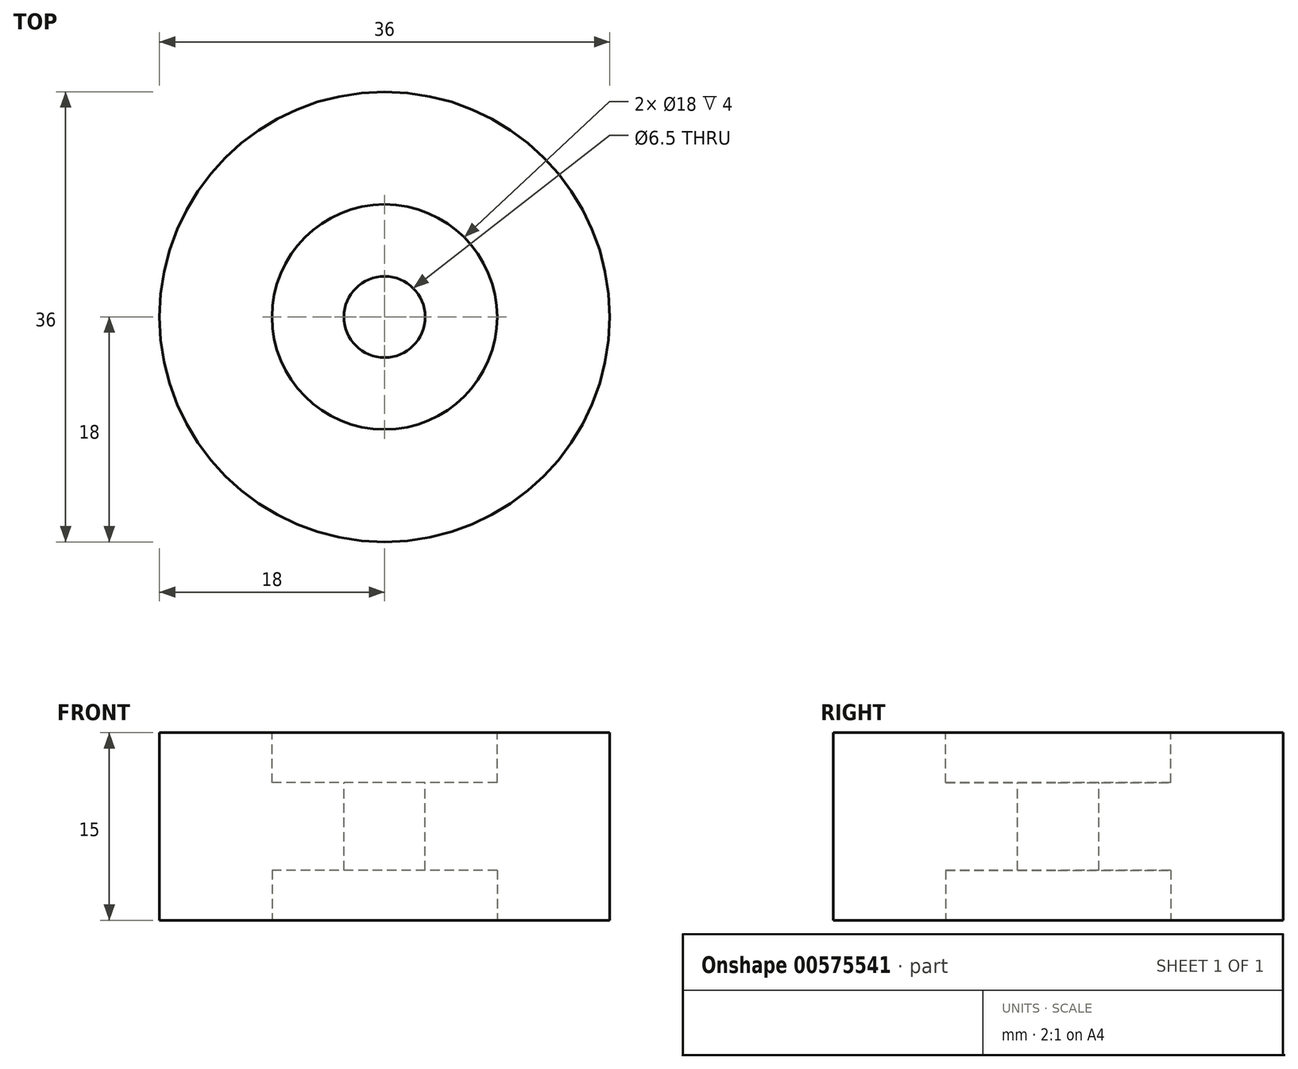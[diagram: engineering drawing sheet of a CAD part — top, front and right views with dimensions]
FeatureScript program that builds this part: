
annotation { "Feature Type Name" : "Feature", "Feature Type Description" : "" }
export const myFeature = defineFeature(function(context is Context, id is Id, definition is map)
    precondition{}
    {
        {
            var Q0;
            Q0=qCreatedBy(makeId("Top.planeOp"),FACE);
            var sketch = newSketch(context, id + "F0", { "sketchPlane" : qUnion([Q0])});
            skCircle(sketch, "E0", {"center": v(0, 0) * mm, "radius": 18 * mm});
            skSolve(sketch);
        }
        {
            var Q0;
            Q0=makeQuery(id+"F0.imprint","IMPRINT",FACE,{"disambiguationData":[TD([[makeQuery(id+"F0.imprint","IMPRINT",EDGE,{"derivedFrom":sQuery(id+"F0.wireOp",EDGE,"E0")}),1.0]])]});
            extrude(context, id + "F1", {"entities" : qUnion([Q0]), "depth" : 15 * mm, "offsetDistance" : 25 * mm});
        }
        {
            var Q0;
            Q0=makeQuery(id+"F1.opExtrude","CAP_FACE",FACE,{"disambiguationData":[OSD([sQuery(id+"F0.wireOp",EDGE,"E0")])],"isStart":false});
            var sketch = newSketch(context, id + "F2", { "sketchPlane" : qUnion([Q0])});
            skCircle(sketch, "E1", {"center": v(0, 0) * mm, "radius": 9 * mm});
            skCircle(sketch, "E2", {"center": v(0, 0) * mm, "radius": 3.25 * mm});
            skSolve(sketch);
        }
        {
            var Q0;
            Q0=makeQuery(id+"F2.imprint","IMPRINT",FACE,{"disambiguationData":[TD([[makeQuery(id+"F2.imprint","IMPRINT",EDGE,{"derivedFrom":sQuery(id+"F2.wireOp",EDGE,"E1")}),1.0]])]});
            var Q1;
            Q1=sQuery(id+"F2.wireOp",EDGE,"E1");
            extrude(context, id + "F3", {"entities" : qUnion([Q0]), "operationType" : NewBodyOperationType.REMOVE, "surfaceEntities" : qUnion([Q1]), "oppositeDirection" : true, "depth" : 4 * mm, "offsetDistance" : 25 * mm});
        }
        {
            var Q0;
            Q0=makeQuery(id+"F2.imprint","IMPRINT",FACE,{"disambiguationData":[TD([[makeQuery(id+"F2.imprint","IMPRINT",EDGE,{"derivedFrom":sQuery(id+"F2.wireOp",EDGE,"E2")}),1.0]])]});
            extrude(context, id + "F4", {"entities" : qUnion([Q0]), "operationType" : NewBodyOperationType.REMOVE, "oppositeDirection" : true, "depth" : 25 * mm, "offsetDistance" : 25 * mm});
        }
        {
            var Q0;
            Q0=makeQuery(id+"F0.imprint","IMPRINT",FACE,{"disambiguationData":[TD([[makeQuery(id+"F0.imprint","IMPRINT",EDGE,{"derivedFrom":sQuery(id+"F0.wireOp",EDGE,"E0")}),1.0]])]});
            var sketch = newSketch(context, id + "F5", { "sketchPlane" : qUnion([Q0])});
            skCircle(sketch, "E3", {"center": v(0, 0) * mm, "radius": 9 * mm});
            skSolve(sketch);
        }
        {
            var Q0;
            Q0=makeQuery(id+"F5.imprint","IMPRINT",FACE,{"disambiguationData":[TD([[makeQuery(id+"F5.imprint","IMPRINT",EDGE,{"derivedFrom":sQuery(id+"F5.wireOp",EDGE,"E3")}),1.0]])]});
            var Q1;
            Q1=sQuery(id+"F5.wireOp",EDGE,"E3");
            extrude(context, id + "F6", {"entities" : qUnion([Q0]), "operationType" : NewBodyOperationType.REMOVE, "surfaceEntities" : qUnion([Q1]), "oppositeDirection" : true, "depth" : -4 * mm, "offsetDistance" : 25 * mm});
        }
    });
